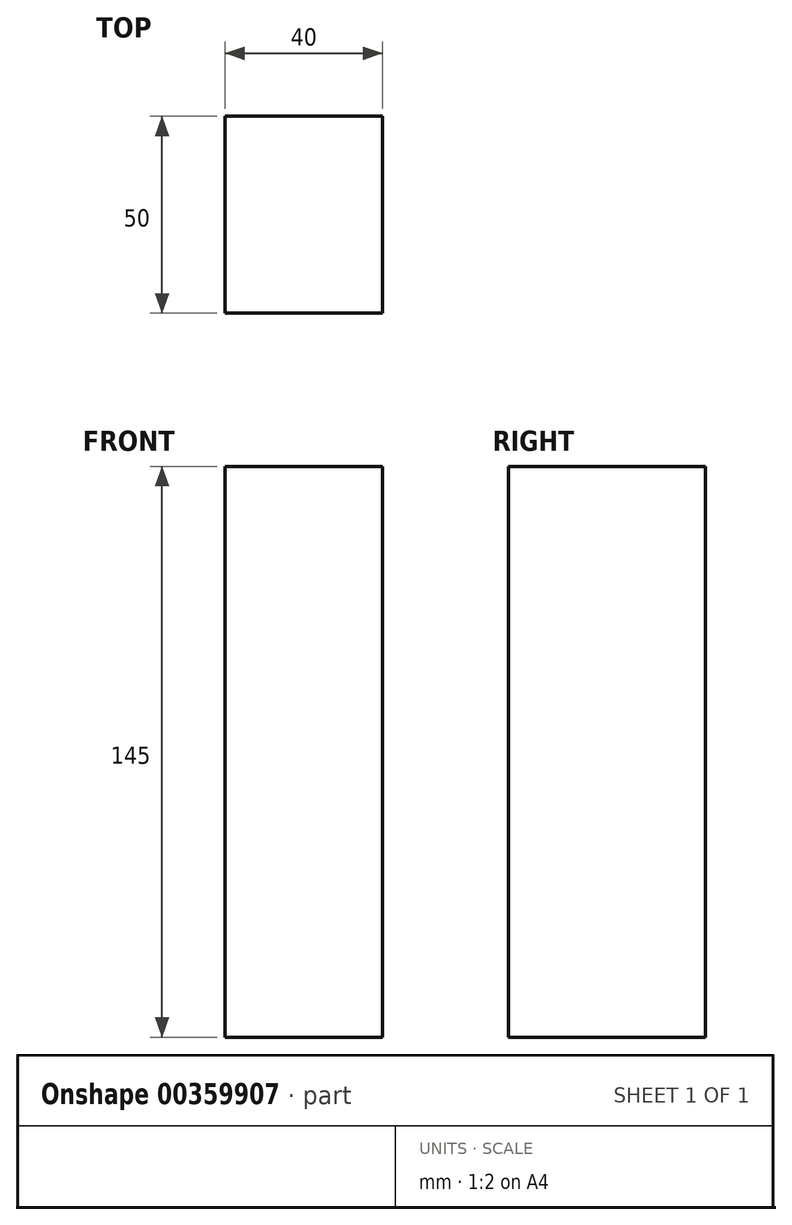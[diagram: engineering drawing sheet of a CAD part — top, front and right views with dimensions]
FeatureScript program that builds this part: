
annotation { "Feature Type Name" : "Feature", "Feature Type Description" : "" }
export const myFeature = defineFeature(function(context is Context, id is Id, definition is map)
    precondition{}
    {
        {
            var Q0;
            Q0=qCreatedBy(makeId("Top.planeOp"),FACE);
            var sketch = newSketch(context, id + "F0", { "sketchPlane" : qUnion([Q0])});
            skLineSegment(sketch, "E0.bottom", {"start": v(-20, 25) * mm, "end": v(20, 25) * mm});
            skLineSegment(sketch, "E0.top", {"start": v(-20, -25) * mm, "end": v(20, -25) * mm});
            skLineSegment(sketch, "E0.left", {"start": v(-20, 25) * mm, "end": v(-20, -25) * mm});
            skLineSegment(sketch, "E0.right", {"start": v(20, 25) * mm, "end": v(20, -25) * mm});
            skPoint(sketch, "E0.middle", {"position": v(0, 0) * mm});
            skSolve(sketch);
        }
        {
            var Q0;
            Q0=makeQuery(id+"F0.imprint","IMPRINT",FACE,{"disambiguationData":[TD([[makeQuery(id+"F0.imprint","IMPRINT",EDGE,{"derivedFrom":sQuery(id+"F0.wireOp",EDGE,"E0.bottom")}),-1.0]])]});
            extrude(context, id + "F1", {"entities" : qUnion([Q0]), "depth" : 145 * mm});
        }
    });
